# Revit family: LSM4421
name_source: partatom
category: Luminarias
units: mm (PartAtom-declared; Revit-internal decimal feet)

## family parameters
Compartido = Sí
Corte con vacíos al cargar = No
Cota de conector redondo = Diámetro de uso
Origen de luz = No
Punto de cálculo de habitación = No
Se basa en plano de trabajo = Sí
Siempre vertical = No
Tipo de pieza = Normal

## types (1)
- PERFIL_LSM4421
    Clip de Sujecion LSM-4424 = 4
    Conexion Lineal LSM-4425 = 1
    Descripción = PERFIL DE ALUMINIO CON DIFUSOR LECHOSO, PARA ALOJAR DOS TIRAS LUMINOSAS DE HASTA 23.15MM DE ANCHO. INSTALACION SOBRE SUPERFICIES PARA CONTORNEAR MUROS, PERFIL DE CLIP MONTADO. IDEAL PARA ATENUAR EL BRILLO E INCORPORAR LA LUZ AL AMBIENTE.PRESENTACION DE 1 METRO, REQUEIRE ACCESORIOS COMO DIFUSOR, TAPA FINAL (CONSIDERAR 1 POR SEGMENTO DE PERFIL), CLIPS DE SUJECION LINEAL (CONSIDERAR 4 PZAS POR 1M DE PERFIL) Y CONEXIÓN LINEAL.DEMAS ACCESORIOS PARA CONTINUIDAD EN ESCUADRAS VERTICALES Y HORIZONTALES CUANTIFICADAS POR SEPARADO.
    Difusor LSM-4422 = 1
    Elevación por defecto = 1219 mm
    Fabricante = BRILLANT
    Longitud = 1000 mm  [stored 3.28084 ft]
    Modelo = LSM4421
    Tapa Final LSM-4423 = 1

note: [stored X ft] marks values corroborated as IEEE doubles in the binary element streams (Revit-internal decimal feet)

## geometry (parser evidence)
native form markers: Blend x2
no freeform markers — native parametric forms only
